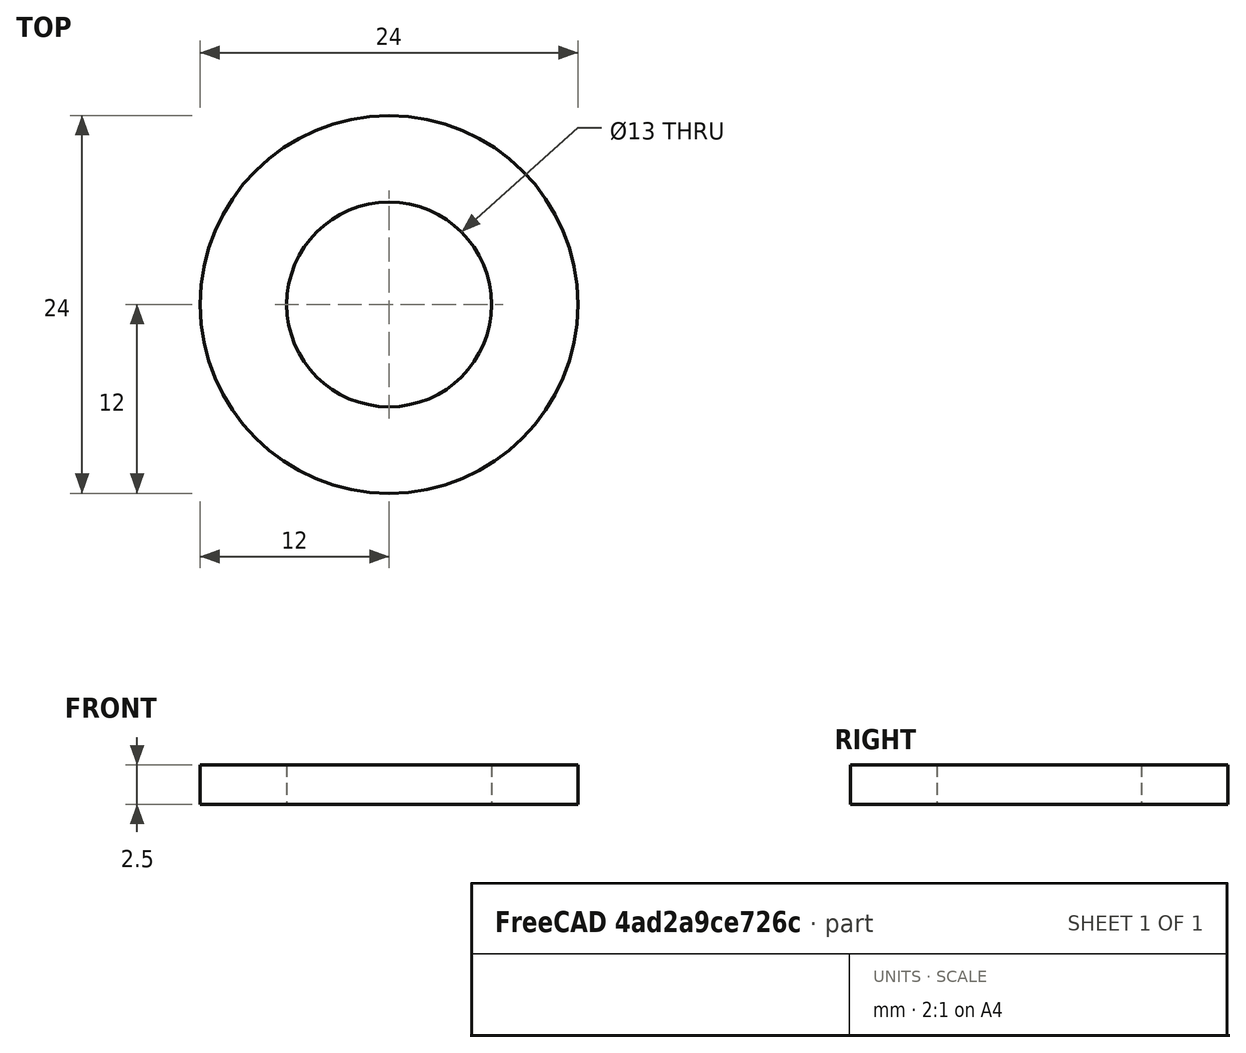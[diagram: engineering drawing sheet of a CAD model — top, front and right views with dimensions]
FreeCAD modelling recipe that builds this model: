
FCSTD DOCUMENT  (FreeCAD 0.14R3700 (Git))
Label: Scheibe DIN 125 - A 13
License: CC-BY 3.0
LicenseURL: http://creativecommons.org/licenses/by/3.0/
objects: Sketcher::SketchObject×1, PartDesign::Revolution×1, Part::Feature×1
note: 4 computed .brp shape members not serialized (recipe doc carries the construction recipe); baked Part::Feature solids carry a one-line shape summary decoded from their .brp

FEATURE [Sketcher::SketchObject] Sketch
  Placement = pos=(0,0,0) rot=(0.57735,0.57735,0.57735;2.0944rad)
  sketch-geometry (4):
    g0: LineSegment StartX=6.5 StartY=0 StartZ=0 EndX=12 EndY=0 EndZ=0
    g1: LineSegment StartX=12 StartY=0 StartZ=0 EndX=12 EndY=2.5 EndZ=0
    g2: LineSegment StartX=12 StartY=2.5 StartZ=0 EndX=6.5 EndY=2.5 EndZ=0
    g3: LineSegment StartX=6.5 StartY=2.5 StartZ=0 EndX=6.5 EndY=0 EndZ=0
  constraints (12):
    c: Coincident(g0,g1)
    c: Coincident(g1,g2)
    c: Coincident(g2,g3)
    c: Coincident(g3,g0)
    c: Horizontal(g0)
    c: Horizontal(g2)
    c: Vertical(g1)
    c: Vertical(g3)
    c: PointOnObject(g0,g-1)
    c: DistanceY(g1) = 2.5
    c: DistanceX(g-1,g2) = 6.5
    c: DistanceX(g-1,g1) = 12
FEATURE [PartDesign::Revolution] Revolution  label="Scheibe DIN 125 - A 13 #"
  Angle = 360
  Axis = (0,0,1)
  Base = (0,0,0)
  Placement = pos=(0,0,0) rot=(0.57735,0.57735,0.57735;2.0944rad)
  ReferenceAxis = -> Sketch [V_Axis]
  Reversed = true
  Sketch = -> Sketch
FEATURE [Part::Feature] Revolution001  label="Scheibe DIN 125 - A 13 #001"
  Placement = pos=(0,0,0) rot=(0.57735,0.57735,0.57735;2.0944rad)
  shape: bbox 24 x 24 x 2.5 mm, 4 faces (baked)
